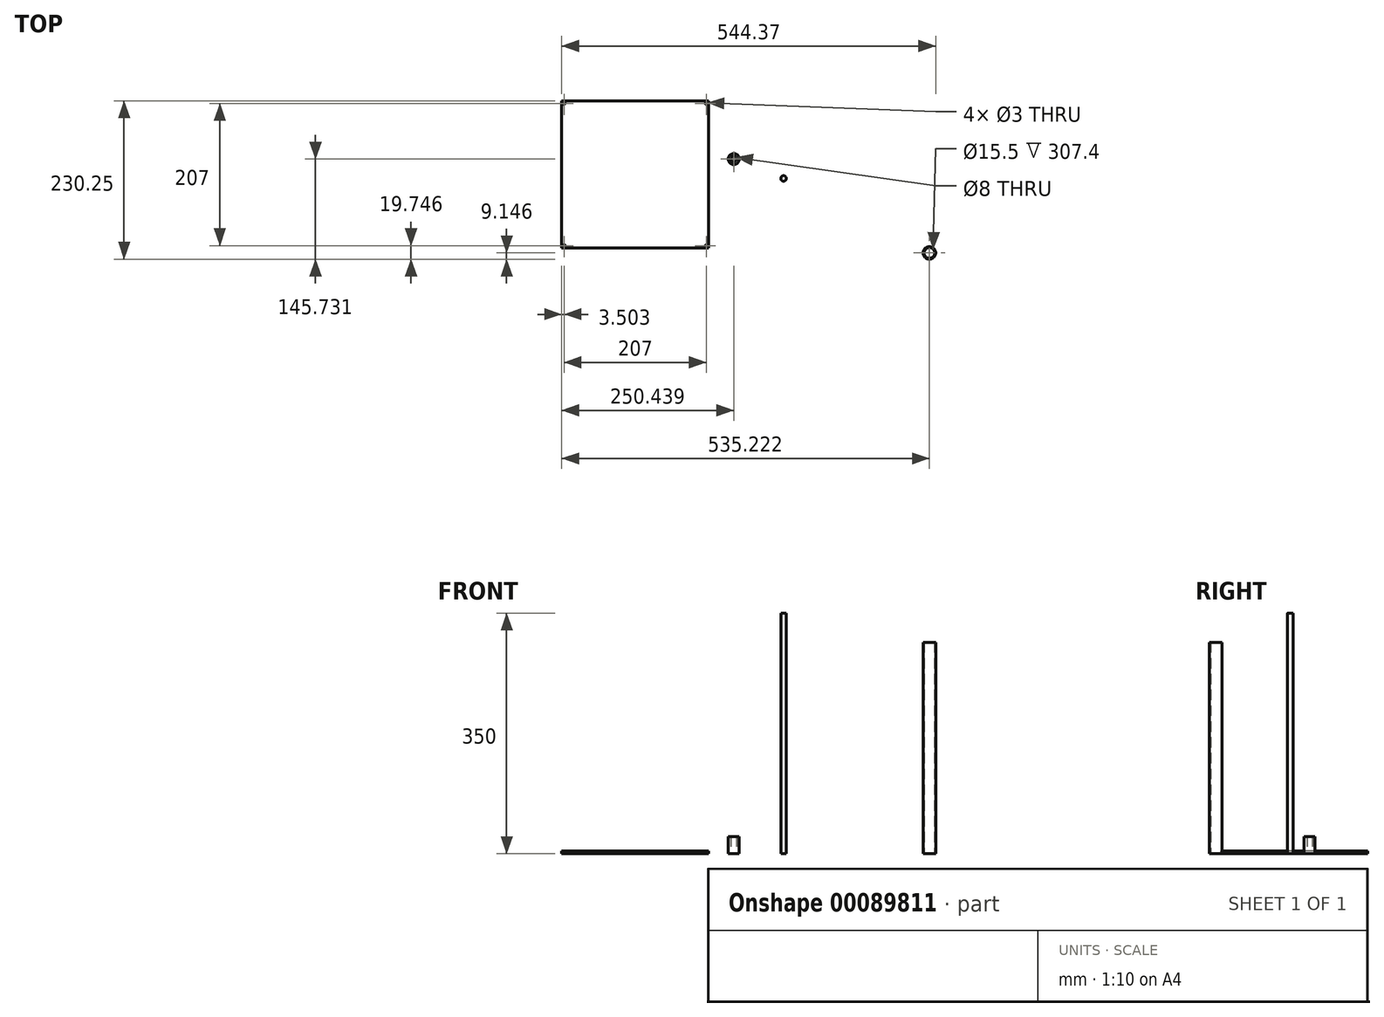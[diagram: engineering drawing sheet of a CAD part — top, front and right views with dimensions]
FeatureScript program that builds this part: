
annotation { "Feature Type Name" : "Feature", "Feature Type Description" : "" }
export const myFeature = defineFeature(function(context is Context, id is Id, definition is map)
    precondition{}
    {
        {
            var Q0;
            Q0=qCreatedBy(makeId("Top.planeOp"),FACE);
            var sketch = newSketch(context, id + "F0", { "sketchPlane" : qUnion([Q0])});
            skCircle(sketch, "E0", {"center": v(-45.57, 33.63) * mm, "radius": 8 * mm});
            skCircle(sketch, "E1", {"center": v(-45.57, 33.63) * mm, "radius": 4 * mm});
            skCircle(sketch, "E2", {"center": v(26.94, 5.42) * mm, "radius": 4 * mm});
            skLineSegment(sketch, "E3.bottom", {"start": v(-296, 118.15) * mm, "end": v(-82, 118.15) * mm});
            skLineSegment(sketch, "E3.top", {"start": v(-296, -95.85) * mm, "end": v(-82, -95.85) * mm});
            skLineSegment(sketch, "E3.left", {"start": v(-296, 118.15) * mm, "end": v(-296, -95.85) * mm});
            skLineSegment(sketch, "E3.right", {"start": v(-82, 118.15) * mm, "end": v(-82, -95.85) * mm});
            skCircle(sketch, "E4", {"center": v(-85.5, 114.65) * mm, "radius": 1.5 * mm});
            skCircle(sketch, "E5", {"center": v(-292.5, 114.65) * mm, "radius": 1.5 * mm});
            skCircle(sketch, "E6", {"center": v(-292.5, -92.35) * mm, "radius": 1.5 * mm});
            skCircle(sketch, "E7", {"center": v(-85.5, -92.35) * mm, "radius": 1.5 * mm});
            skCircle(sketch, "E8", {"center": v(239.21, -102.95) * mm, "radius": 9.15 * mm});
            skCircle(sketch, "E9", {"center": v(239.21, -102.95) * mm, "radius": 7.75 * mm});
            skSolve(sketch);
        }
        {
            var Q0;
            Q0=makeQuery(id+"F0.imprint","IMPRINT",FACE,{"disambiguationData":[TD([[makeQuery(id+"F0.imprint","IMPRINT",EDGE,{"derivedFrom":sQuery(id+"F0.wireOp",EDGE,"E0")}),1.0]])]});
            extrude(context, id + "F1", {"entities" : qUnion([Q0]), "depth" : 25 * mm});
        }
        {
            var Q0;
            Q0=makeQuery(id+"F0.imprint","IMPRINT",FACE,{"disambiguationData":[TD([[makeQuery(id+"F0.imprint","IMPRINT",EDGE,{"derivedFrom":sQuery(id+"F0.wireOp",EDGE,"E2")}),1.0]])]});
            extrude(context, id + "F2", {"entities" : qUnion([Q0]), "depth" : 350 * mm});
        }
        {
            var Q0;
            Q0=makeQuery(id+"F0.imprint","IMPRINT",FACE,{"disambiguationData":[TD([[makeQuery(id+"F0.imprint","IMPRINT",EDGE,{"derivedFrom":sQuery(id+"F0.wireOp",EDGE,"E3.bottom")}),-1.0]])]});
            extrude(context, id + "F3", {"entities" : qUnion([Q0]), "depth" : 4 * mm});
        }
        {
            var Q0;
            Q0=makeQuery(id+"F0.imprint","IMPRINT",FACE,{"disambiguationData":[TD([[makeQuery(id+"F0.imprint","IMPRINT",EDGE,{"derivedFrom":sQuery(id+"F0.wireOp",EDGE,"E8")}),1.0]])]});
            extrude(context, id + "F4", {"entities" : qUnion([Q0]), "depth" : (350 - (18.3 * 2) - (3 * 2)) * mm});
        }
    });
